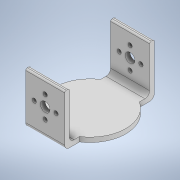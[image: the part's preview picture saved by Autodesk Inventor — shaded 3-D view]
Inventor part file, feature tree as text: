
AUTODESK INVENTOR PART (.ipt)
format: ipt  version: 2022 (Build 260153000, 153)  size: 465,408 bytes
history: native  units: mm
features: fillet x8, sketch x8, extrude x7, other x3, pattern_circular x1, mirror x1, revolve x1, projected_geometry x1
ambient origin geometry x8: Origin, YZ Plane, XZ Plane, XY Plane, X Axis, Y Axis, Z Axis, Center Point
bodies: Body1 (feature_tree)
feature tree (30):
  other  "Твердое тело1"
  extrude  "Выдавливание1"  Depth=51.5mm
  extrude  "Выдавливание2"  Depth=25.0mm
  fillet  "Сопряжение1"  Radius=45.8mm
  extrude  "Выдавливание3"  Depth=3.0mm TaperAngle=0.0deg
  extrude  "Выдавливание4"  Depth=37.8mm
  fillet  "Сопряжение4"  Radius=2.0mm
  fillet  "Сопряжение10"  Radius=1.0mm
  pattern_circular  "Круговой массив1"  [2 undecoded]
  fillet  "Сопряжение5"  Radius=24.7mm
  other  "РабПлоскость1"
  extrude  "Выдавливание5"  Depth=7.0mm TaperAngle=0.0deg
  fillet  "Сопряжение6"  Radius=10.0mm
  fillet  "Сопряжение7"  Radius=0.7mm
  mirror  "Зеркальное отражение1"
  fillet  "Сопряжение8"  Radius=80.0mm
  extrude  "Выдавливание6"  Depth=0.2mm
  extrude  "Выдавливание7"  Depth=30.0mm
  fillet  "Сопряжение9"  Radius=6.2mm
  other  "РабПлоскость2"
  revolve  "Вращение1"
  sketch  "Эскиз1"
  sketch  "Эскиз2"
  sketch  "Эскиз3"
  sketch  "Эскиз4"
  sketch  "Эскиз6"
  sketch  "Эскиз7"
  sketch  "Эскиз8"
  sketch  "Эскиз9"
  projected_geometry  "Спроецированная петля1"
note: 2 required parameter values undecoded (feature->parameter linkage not recoverable at this tier; creation-order binding heuristic only, values carry confidence <= 0.55)
